# Revit family: equip-sink-elkay-single-lustertone-llvr1916
name_source: partatom
category: Generic Models
units: mm (PartAtom-declared; Revit-internal decimal feet)

## family parameters
Always vertical = Yes
Can host rebar = No
Cut with Voids When Loaded = No
Part Type = Normal
Room Calculation Point = No
Round Connector Dimension = Use Diameter
Shared = No
Work Plane-Based = No

## types (4) — shared parameters
2D Hole 1 = No
2D Hole 2 = No
2D Hole 3 = No
2D Hole 4 = No
2D Hole 5 = No
Description = Lustertone Sink Sink
Drain Location = 0' - 4"
Faucet Hole CL = 0' - 2 1/2"
Hole 1 Top = 0' - 2 1/8"
Installation Sheet URL = http://www.elkayusa.com
Manufacturer = Elkay Manufacturing
Model = LLVR1916
Sink Depth = 0' - 6"
Sink Ledge Back Width = 0' - 4"
Sink Ledge Front Width = 0' - 1 5/8"
Sink Ledge Sides Width = 0' - 1 3/4"
Sink Length = 1' - 7"
Sink Material = Metal - Steel - Stainless - Chrome
Sink Width = 1' - 5"
Specification Sheet URL = http://www.elkayusa.com
URL = www.elkayusa.com

## per-type parameters (varying)
| type | Hole 1 from CL | Hole 1 to 2 | Hole 1 to 3 | Hole 2 Top | Hole 3 Top |
| Hole 1 | 0' - 0" | 0' - 2" | 0' - 4" | 0' - 1 1/2" | 0' - 1 1/2" |
| Hole 2 | 0' - 2" | 0' - 4" | 0' - 6" | 0' - 2 1/8" | 0' - 1 1/2" |
| Hole 3 | 0' - 4" | 0' - 4" | 0' - 8" | 0' - 2 1/8" | 0' - 2 1/8" |
| Hole 3 CenterSet | 0' - 2" | 0' - 2" | 0' - 4" | 0' - 2 1/8" | 0' - 2 1/8" |

## geometry (parser evidence)
native form markers: Sweep x6
no freeform markers — native parametric forms only
